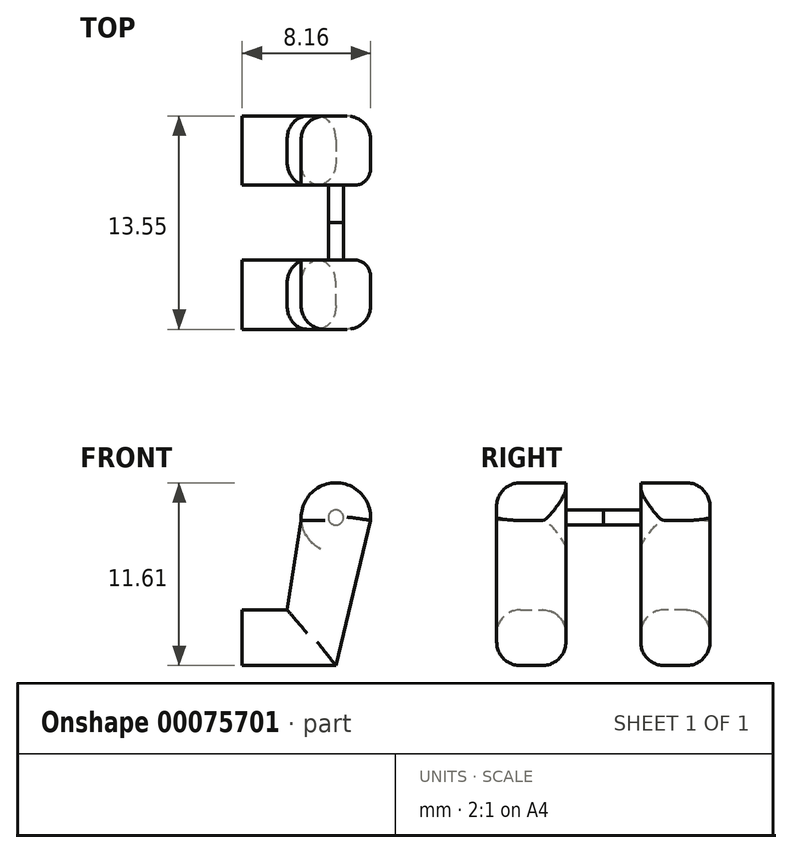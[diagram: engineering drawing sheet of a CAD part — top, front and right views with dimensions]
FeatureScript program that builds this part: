
annotation { "Feature Type Name" : "Feature", "Feature Type Description" : "" }
export const myFeature = defineFeature(function(context is Context, id is Id, definition is map)
    precondition{}
    {
        {
            var Q0;
            Q0=qCreatedBy(makeId("Front.planeOp"),FACE);
            var sketch = newSketch(context, id + "F0", { "sketchPlane" : qUnion([Q0])});
            skCircle(sketch, "E0", {"center": v(0, 7.05) * mm, "radius": 2.2 * mm});
            skLineSegment(sketch, "E1", {"start": v(-2.2, 6.87) * mm, "end": v(2.2, 6.87) * mm});
            skLineSegment(sketch, "E2", {"start": v(2.2, 6.87) * mm, "end": v(0, -2.35) * mm});
            skLineSegment(sketch, "E3", {"start": v(0, -2.35) * mm, "end": v(-5.95, -2.35) * mm});
            skLineSegment(sketch, "E4", {"start": v(-5.95, -2.35) * mm, "end": v(-5.95, 1.2) * mm});
            skLineSegment(sketch, "E5", {"start": v(-5.95, 1.2) * mm, "end": v(-3.1, 1.2) * mm});
            skLineSegment(sketch, "E6", {"start": v(-3.1, 1.2) * mm, "end": v(-2.2, 6.87) * mm});
            skSolve(sketch);
        }
        {
            var Q0;
            {var subQ0=sQuery(id+"F0.wireOp",EDGE,"E1");Q0=makeQuery(id+"F0.imprint","IMPRINT",FACE,{"disambiguationData":[TD([[makeQuery(id+"F0.imprint","IMPRINT",EDGE,{"derivedFrom":subQ0}),-1.0]])]});}
            var Q1;
            {var subQ0=sQuery(id+"F0.wireOp",EDGE,"E1");Q1=makeQuery(id+"F0.imprint","IMPRINT",FACE,{"disambiguationData":[TD([[makeQuery(id+"F0.imprint","IMPRINT",EDGE,{"derivedFrom":subQ0}),1.0]])]});}
            var Q2;
            {var subQ0=sQuery(id+"F0.wireOp",EDGE,"E3");Q2=makeQuery(id+"F0.imprint","IMPRINT",FACE,{"disambiguationData":[TD([[makeQuery(id+"F0.imprint","IMPRINT",EDGE,{"derivedFrom":subQ0}),-1.0]])]});}
            extrude(context, id + "F1", {"entities" : qUnion([Q0, Q1, Q2]), "depth" : 4.4 * mm});
        }
        {
            var Q0;
            Q0=makeQuery(id+"F1.opExtrude","CAP_EDGE",EDGE,{"disambiguationData":[OSD([sQuery(id+"F0.wireOp",EDGE,"E3")])],"isStart":false});
            var Q1;
            Q1=makeQuery(id+"F1.opExtrude","CAP_EDGE",EDGE,{"disambiguationData":[OSD([sQuery(id+"F0.wireOp",EDGE,"E5")])],"isStart":false});
            var Q2;
            Q2=makeQuery(id+"F1.opExtrude","CAP_EDGE",EDGE,{"disambiguationData":[OSD([sQuery(id+"F0.wireOp",EDGE,"E6")])],"isStart":false});
            var Q3;
            Q3=makeQuery(id+"F1.opExtrude","CAP_EDGE",EDGE,{"disambiguationData":[OSD([sQuery(id+"F0.wireOp",EDGE,"E2")])],"isStart":false});
            var Q4;
            Q4=makeQuery(id+"F1.opExtrude","CAP_EDGE",EDGE,{"disambiguationData":[OSD([sQuery(id+"F0.wireOp",EDGE,"E0")])],"isStart":false});
            fillet(context, id + "F2", {"entities" : qUnion([Q0, Q1, Q2, Q3, Q4]), "radius" : 1.5 * mm, "tangentPropagation" : true, "allowEdgeOverflow" : false});
        }
        {
            var Q0;
            Q0=makeQuery(id+"F1.opExtrude","CAP_EDGE",EDGE,{"disambiguationData":[OSD([sQuery(id+"F0.wireOp",EDGE,"E2")])],"isStart":true});
            var Q1;
            Q1=makeQuery(id+"F1.opExtrude","CAP_EDGE",EDGE,{"disambiguationData":[OSD([sQuery(id+"F0.wireOp",EDGE,"E6")])],"isStart":true});
            var Q2;
            Q2=makeQuery(id+"F1.opExtrude","CAP_EDGE",EDGE,{"disambiguationData":[OSD([sQuery(id+"F0.wireOp",EDGE,"E5")])],"isStart":true});
            var Q3;
            Q3=makeQuery(id+"F1.opExtrude","CAP_EDGE",EDGE,{"disambiguationData":[OSD([sQuery(id+"F0.wireOp",EDGE,"E3")])],"isStart":true});
            fillet(context, id + "F3", {"entities" : qUnion([Q0, Q1, Q2, Q3]), "radius" : 1.5 * mm, "tangentPropagation" : true, "allowEdgeOverflow" : false});
        }
        {
            var Q0;
            Q0=makeQuery(id+"F1.opExtrude","CAP_FACE",FACE,{"disambiguationData":[OSD([sQuery(id+"F0.wireOp",EDGE,"E0"),sQuery(id+"F0.wireOp",EDGE,"E2"),sQuery(id+"F0.wireOp",EDGE,"E3"),sQuery(id+"F0.wireOp",EDGE,"E4"),sQuery(id+"F0.wireOp",EDGE,"E5"),sQuery(id+"F0.wireOp",EDGE,"E6")])],"isStart":true});
            var sketch = newSketch(context, id + "F4", { "sketchPlane" : qUnion([Q0])});
            skCircle(sketch, "E7", {"center": v(0, 7.05) * mm, "radius": 0.48 * mm});
            skSolve(sketch);
        }
        {
            var Q0;
            Q0=makeQuery(id+"F4.imprint","IMPRINT",FACE,{"disambiguationData":[TD([[makeQuery(id+"F4.imprint","IMPRINT",EDGE,{"derivedFrom":sQuery(id+"F4.wireOp",EDGE,"E7")}),1.0]])]});
            var Q1;
            Q1=sQuery(id+"F4.wireOp",EDGE,"E7");
            extrude(context, id + "F5", {"entities" : qUnion([Q0]), "operationType" : NewBodyOperationType.ADD, "surfaceEntities" : qUnion([Q1]), "depth" : 2.37 * mm});
        }
        {
            var Q0;
            Q0=makeQuery(id+"F1.opExtrude","SWEPT_BODY",BODY,{"disambiguationData":[OSD([sQuery(id+"F0.wireOp",EDGE,"E0"),sQuery(id+"F0.wireOp",EDGE,"E2"),sQuery(id+"F0.wireOp",EDGE,"E3"),sQuery(id+"F0.wireOp",EDGE,"E4"),sQuery(id+"F0.wireOp",EDGE,"E5"),sQuery(id+"F0.wireOp",EDGE,"E6")])]});
            var Q1;
            Q1=makeQuery(id+"F5.opExtrude","CAP_FACE",FACE,{"disambiguationData":[OSD([sQuery(id+"F4.wireOp",EDGE,"E7")])],"isStart":false});
            mirror(context, id + "F6", {"entities" : qUnion([Q0]), "mirrorPlane" : qUnion([Q1])});
        }
    });
